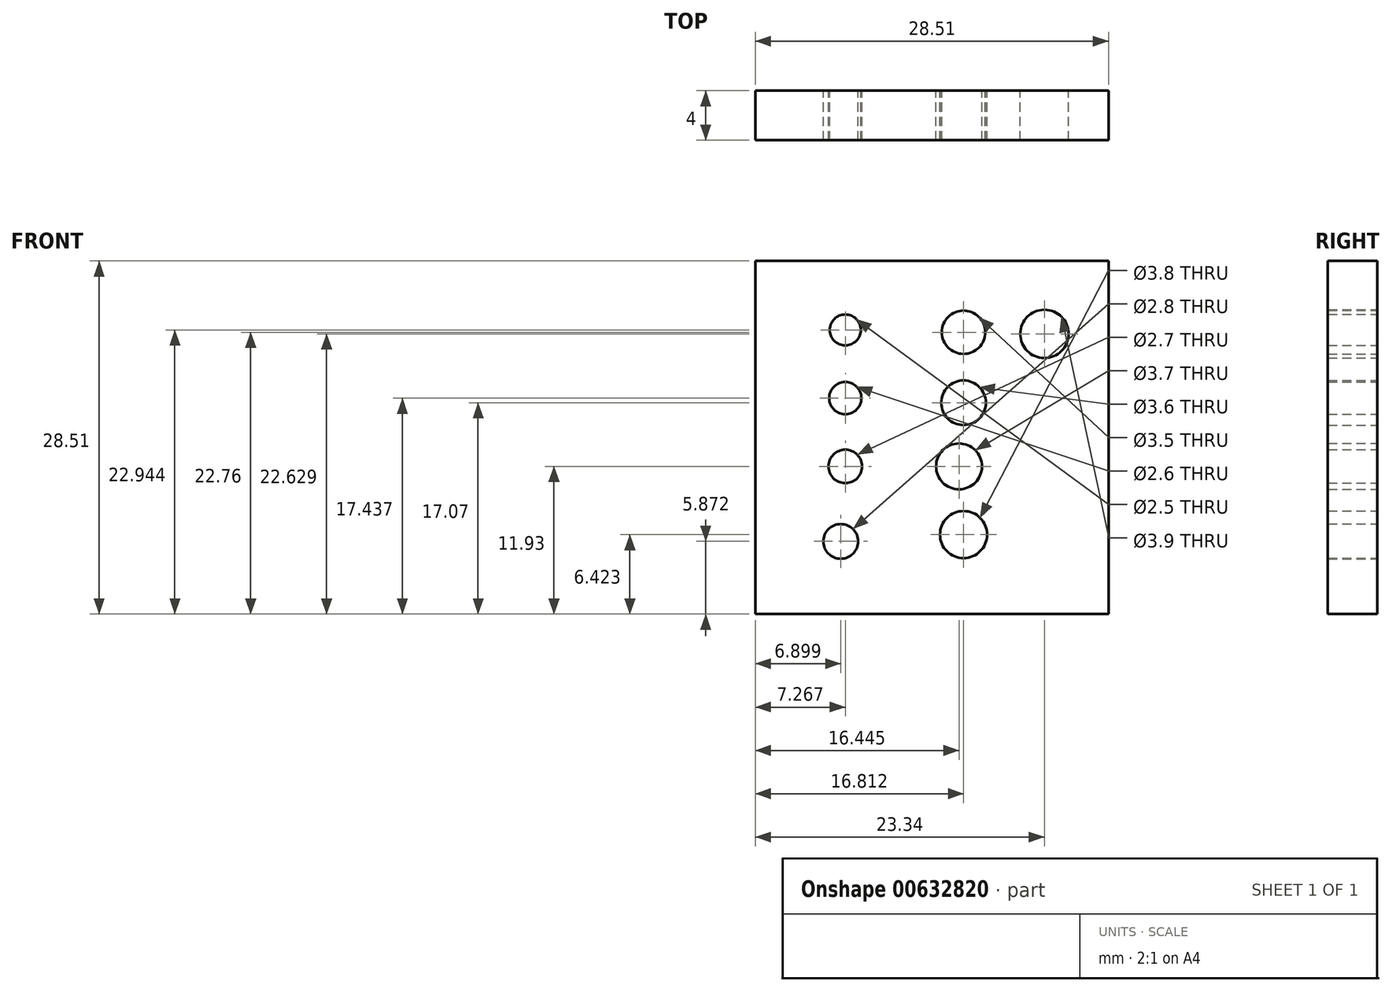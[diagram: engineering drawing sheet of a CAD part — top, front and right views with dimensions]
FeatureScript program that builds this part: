
annotation { "Feature Type Name" : "Feature", "Feature Type Description" : "" }
export const myFeature = defineFeature(function(context is Context, id is Id, definition is map)
    precondition{}
    {
        {
            var Q0;
            Q0=qCreatedBy(makeId("Front.planeOp"),FACE);
            var sketch = newSketch(context, id + "F0", { "sketchPlane" : qUnion([Q0])});
            skLineSegment(sketch, "E0.bottom", {"start": v(0, 0) * mm, "end": v(28.51, 0) * mm});
            skLineSegment(sketch, "E0.top", {"start": v(0, 28.51) * mm, "end": v(28.51, 28.51) * mm});
            skLineSegment(sketch, "E0.left", {"start": v(0, 0) * mm, "end": v(0, 28.5) * mm});
            skLineSegment(sketch, "E0.right", {"start": v(28.5, 0) * mm, "end": v(28.5, 28.51) * mm});
            skCircle(sketch, "E1", {"center": v(7.27, 22.94) * mm, "radius": 1.25 * mm});
            skPoint(sketch, "E1.centerSnap0", {"position": v(0, 14.26) * mm});
            skCircle(sketch, "E2", {"center": v(7.27, 17.44) * mm, "radius": 1.3 * mm});
            skCircle(sketch, "E3", {"center": v(16.81, 22.76) * mm, "radius": 1.75 * mm});
            skCircle(sketch, "E4", {"center": v(16.81, 17.07) * mm, "radius": 1.8 * mm});
            skCircle(sketch, "E5", {"center": v(16.44, 11.93) * mm, "radius": 1.85 * mm});
            skCircle(sketch, "E6", {"center": v(7.27, 11.93) * mm, "radius": 1.35 * mm});
            skCircle(sketch, "E7", {"center": v(6.9, 5.87) * mm, "radius": 1.4 * mm});
            skCircle(sketch, "E8", {"center": v(16.81, 6.42) * mm, "radius": 1.9 * mm});
            skCircle(sketch, "E9", {"center": v(23.34, 22.63) * mm, "radius": 1.95 * mm});
            skSolve(sketch);
        }
        {
            var Q0;
            Q0=makeQuery(id+"F0.imprint","IMPRINT",FACE,{"disambiguationData":[TD([[makeQuery(id+"F0.imprint","IMPRINT",EDGE,{"derivedFrom":sQuery(id+"F0.wireOp",EDGE,"E0.bottom")}),1.0]])]});
            extrude(context, id + "F1", {"entities" : qUnion([Q0]), "depth" : 4 * mm, "offsetDistance" : 25 * mm});
        }
    });
